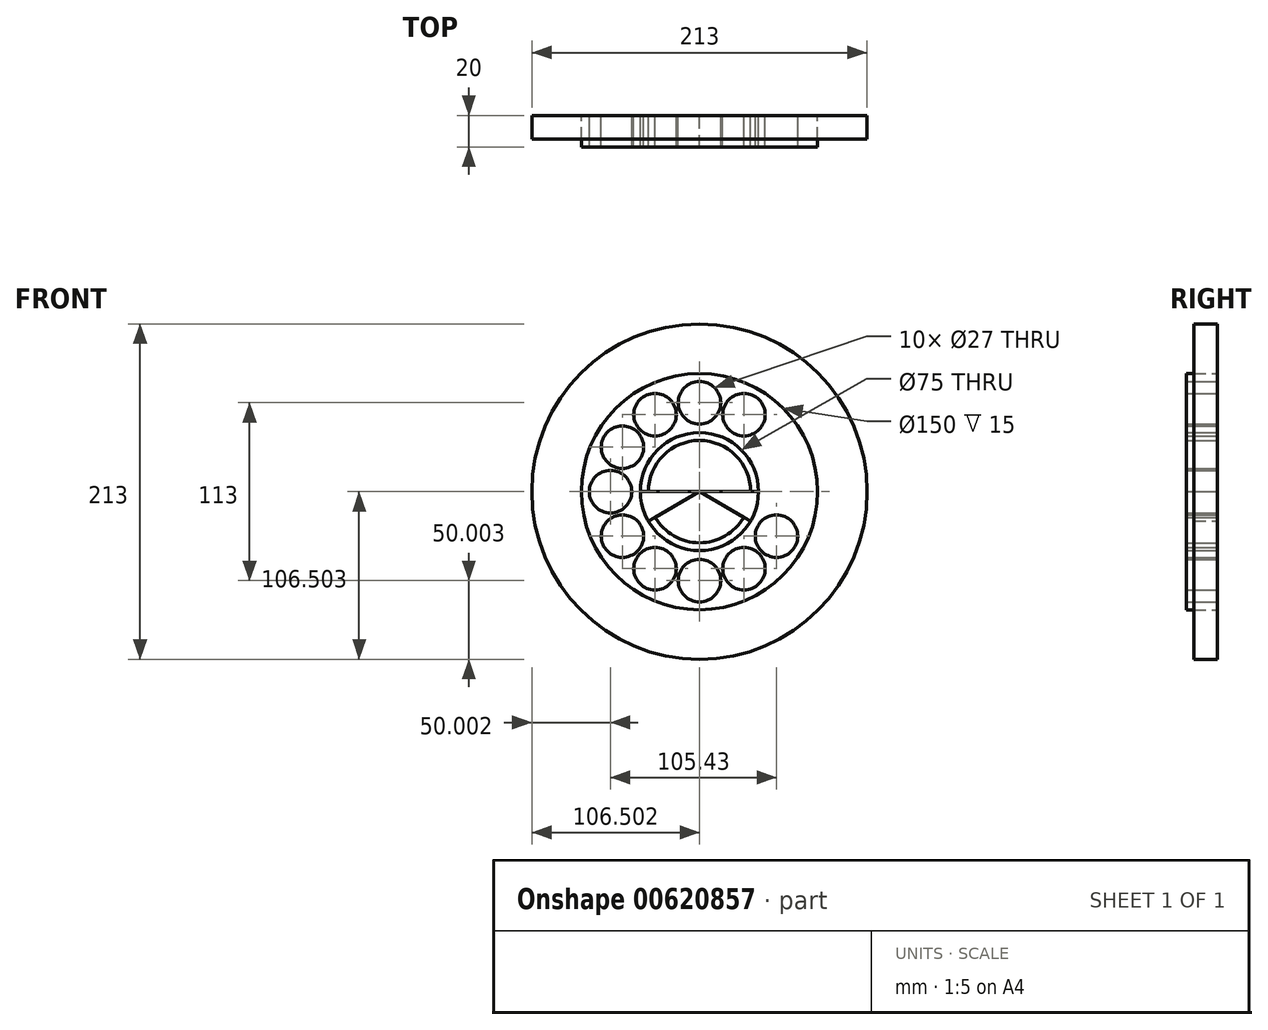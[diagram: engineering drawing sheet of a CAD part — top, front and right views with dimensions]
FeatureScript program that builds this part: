
annotation { "Feature Type Name" : "Feature", "Feature Type Description" : "" }
export const myFeature = defineFeature(function(context is Context, id is Id, definition is map)
    precondition{}
    {
        {
            var Q0;
            Q0=qCreatedBy(makeId("Front.planeOp"),FACE);
            var sketch = newSketch(context, id + "F0", { "sketchPlane" : qUnion([Q0])});
            skCircle(sketch, "E0", {"center": v(-36.97, 6.73) * mm, "radius": 32.5 * mm});
            skCircle(sketch, "E1", {"center": v(-36.97, 6.73) * mm, "radius": 37.5 * mm});
            skCircle(sketch, "E2", {"center": v(-8.72, 55.66) * mm, "radius": 13.5 * mm});
            skCircle(sketch, "E3", {"center": v(-85.9, 35) * mm, "radius": 13.5 * mm});
            skCircle(sketch, "E4", {"center": v(-85.9, -21.52) * mm, "radius": 13.5 * mm});
            skCircle(sketch, "E5", {"center": v(-8.72, -42.2) * mm, "radius": 13.5 * mm});
            skPoint(sketch, "E6.orphan", {"position": v(-36.97, 76.24) * mm});
            skLineSegment(sketch, "E7.trimOffspring", {"start": v(20.03, 6.73) * mm, "end": v(34.08, 6.73) * mm});
            skLineSegment(sketch, "E8.trimOffspring", {"start": v(-36.97, -30.77) * mm, "end": v(-36.97, -54.77) * mm});
            skPoint(sketch, "E9.trimOffspring.end.orphan", {"position": v(-36.97, -60.9) * mm});
            skLineSegment(sketch, "E10", {"start": v(-36.97, 76.24) * mm, "end": v(-36.97, -60.9) * mm});
            skLineSegment(sketch, "E11", {"start": v(-93.47, 6.73) * mm, "end": v(20.03, 6.73) * mm});
            skLineSegment(sketch, "E12", {"start": v(-36.97, 6.73) * mm, "end": v(-2.84, 65.84) * mm});
            skLineSegment(sketch, "E13", {"start": v(-36.97, 6.73) * mm, "end": v(30.96, 45.95) * mm});
            skLineSegment(sketch, "E14", {"start": v(-36.97, 6.73) * mm, "end": v(33.85, -34.15) * mm});
            skLineSegment(sketch, "E15", {"start": v(-36.98, 6.75) * mm, "end": v(0.56, -58.26) * mm});
            skLineSegment(sketch, "E16", {"start": v(0.56, -58.26) * mm, "end": v(-0.88, -59.19) * mm});
            skLineSegment(sketch, "E17", {"start": v(-36.97, 6.73) * mm, "end": v(-72.36, -54.56) * mm});
            skLineSegment(sketch, "E18", {"start": v(-36.97, 6.73) * mm, "end": v(-98.34, -28.7) * mm});
            skLineSegment(sketch, "E19", {"start": v(-36.97, 6.73) * mm, "end": v(-68.98, 62.19) * mm});
            skLineSegment(sketch, "E20", {"start": v(-36.98, 6.75) * mm, "end": v(-93.97, 39.65) * mm});
            skCircle(sketch, "E21", {"center": v(-36.97, 6.73) * mm, "radius": 56.5 * mm, "construction": true});
            skCircle(sketch, "E22", {"center": v(-65.22, 55.66) * mm, "radius": 13.5 * mm});
            skCircle(sketch, "E23", {"center": v(-36.97, 63.23) * mm, "radius": 13.5 * mm});
            skCircle(sketch, "E24", {"center": v(-36.97, 6.73) * mm, "radius": 106.5 * mm});
            skCircle(sketch, "E25", {"center": v(-36.97, -49.77) * mm, "radius": 13.5 * mm});
            skCircle(sketch, "E26", {"center": v(-65.22, -42.2) * mm, "radius": 13.5 * mm});
            skCircle(sketch, "E27", {"center": v(-93.47, 6.73) * mm, "radius": 13.5 * mm});
            skCircle(sketch, "E28", {"center": v(11.96, -21.52) * mm, "radius": 13.5 * mm});
            skCircle(sketch, "E29", {"center": v(-36.97, 6.73) * mm, "radius": 75 * mm});
            skSolve(sketch);
        }
        {
            var Q0;
            {var subQ0=sQuery(id+"F0.wireOp",EDGE,"E12");var subQ1=sQuery(id+"F0.wireOp",EDGE,"E0");var subQ2=makeQuery(id+"F0.imprint","INTERSECT",VERTEX,{"derivedFrom":[subQ1,subQ0]});Q0=makeQuery(id+"F0.imprint","IMPRINT",FACE,{"disambiguationData":[TD([[makeQuery(id+"F0.imprint","IMPRINT",EDGE,{"disambiguationData":[TD([[subQ2,-1.0]])],"derivedFrom":subQ1}),-1.0]])]});}
            var Q1;
            {var subQ0=sQuery(id+"F0.wireOp",EDGE,"E13");var subQ1=sQuery(id+"F0.wireOp",EDGE,"E0");var subQ2=makeQuery(id+"F0.imprint","INTERSECT",VERTEX,{"derivedFrom":[subQ1,subQ0]});Q1=makeQuery(id+"F0.imprint","IMPRINT",FACE,{"disambiguationData":[TD([[makeQuery(id+"F0.imprint","IMPRINT",EDGE,{"disambiguationData":[TD([[subQ2,-1.0]])],"derivedFrom":subQ1}),-1.0]])]});}
            var Q2;
            {var subQ0=sQuery(id+"F0.wireOp",EDGE,"E13");var subQ1=sQuery(id+"F0.wireOp",EDGE,"E0");var subQ2=makeQuery(id+"F0.imprint","INTERSECT",VERTEX,{"derivedFrom":[subQ1,subQ0]});Q2=makeQuery(id+"F0.imprint","IMPRINT",FACE,{"disambiguationData":[TD([[makeQuery(id+"F0.imprint","IMPRINT",EDGE,{"disambiguationData":[TD([[subQ2,1.0]])],"derivedFrom":subQ1}),-1.0]])]});}
            var Q3;
            {var subQ0=sQuery(id+"F0.wireOp",EDGE,"E10");var subQ1=sQuery(id+"F0.wireOp",EDGE,"E0");var subQ2=makeQuery(id+"F0.imprint","INTERSECT",VERTEX,{"disambiguationData":[OD(0.0)],"derivedFrom":[subQ1,subQ0]});Q3=makeQuery(id+"F0.imprint","IMPRINT",FACE,{"disambiguationData":[TD([[makeQuery(id+"F0.imprint","IMPRINT",EDGE,{"disambiguationData":[TD([[subQ2,-1.0]])],"derivedFrom":subQ1}),-1.0]])]});}
            var Q4;
            {var subQ0=sQuery(id+"F0.wireOp",EDGE,"E19");var subQ1=sQuery(id+"F0.wireOp",EDGE,"E0");var subQ2=makeQuery(id+"F0.imprint","INTERSECT",VERTEX,{"derivedFrom":[subQ1,subQ0]});Q4=makeQuery(id+"F0.imprint","IMPRINT",FACE,{"disambiguationData":[TD([[makeQuery(id+"F0.imprint","IMPRINT",EDGE,{"disambiguationData":[TD([[subQ2,-1.0]])],"derivedFrom":subQ1}),-1.0]])]});}
            var Q5;
            {var subQ0=sQuery(id+"F0.wireOp",EDGE,"E20");var subQ1=sQuery(id+"F0.wireOp",EDGE,"E0");var subQ2=makeQuery(id+"F0.imprint","INTERSECT",VERTEX,{"derivedFrom":[subQ1,subQ0]});Q5=makeQuery(id+"F0.imprint","IMPRINT",FACE,{"disambiguationData":[TD([[makeQuery(id+"F0.imprint","IMPRINT",EDGE,{"disambiguationData":[TD([[subQ2,-1.0]])],"derivedFrom":subQ1}),-1.0]])]});}
            var Q6;
            {var subQ0=sQuery(id+"F0.wireOp",EDGE,"E11");var subQ1=sQuery(id+"F0.wireOp",EDGE,"E0");var subQ2=makeQuery(id+"F0.imprint","INTERSECT",VERTEX,{"disambiguationData":[OD(1.0)],"derivedFrom":[subQ1,subQ0]});Q6=makeQuery(id+"F0.imprint","IMPRINT",FACE,{"disambiguationData":[TD([[makeQuery(id+"F0.imprint","IMPRINT",EDGE,{"disambiguationData":[TD([[subQ2,-1.0]])],"derivedFrom":subQ1}),-1.0]])]});}
            var Q7;
            {var subQ0=sQuery(id+"F0.wireOp",EDGE,"E18");var subQ1=sQuery(id+"F0.wireOp",EDGE,"E0");var subQ2=makeQuery(id+"F0.imprint","INTERSECT",VERTEX,{"derivedFrom":[subQ1,subQ0]});Q7=makeQuery(id+"F0.imprint","IMPRINT",FACE,{"disambiguationData":[TD([[makeQuery(id+"F0.imprint","IMPRINT",EDGE,{"disambiguationData":[TD([[subQ2,-1.0]])],"derivedFrom":subQ1}),-1.0]])]});}
            var Q8;
            {var subQ0=sQuery(id+"F0.wireOp",EDGE,"E17");var subQ1=sQuery(id+"F0.wireOp",EDGE,"E0");var subQ2=makeQuery(id+"F0.imprint","INTERSECT",VERTEX,{"derivedFrom":[subQ1,subQ0]});Q8=makeQuery(id+"F0.imprint","IMPRINT",FACE,{"disambiguationData":[TD([[makeQuery(id+"F0.imprint","IMPRINT",EDGE,{"disambiguationData":[TD([[subQ2,-1.0]])],"derivedFrom":subQ1}),-1.0]])]});}
            var Q9;
            {var subQ0=sQuery(id+"F0.wireOp",EDGE,"E10");var subQ1=sQuery(id+"F0.wireOp",EDGE,"E0");var subQ2=makeQuery(id+"F0.imprint","INTERSECT",VERTEX,{"disambiguationData":[OD(1.0)],"derivedFrom":[subQ1,subQ0]});Q9=makeQuery(id+"F0.imprint","IMPRINT",FACE,{"disambiguationData":[TD([[makeQuery(id+"F0.imprint","IMPRINT",EDGE,{"disambiguationData":[TD([[subQ2,-1.0]])],"derivedFrom":subQ1}),-1.0]])]});}
            var Q10;
            {var subQ0=sQuery(id+"F0.wireOp",EDGE,"E11");var subQ1=sQuery(id+"F0.wireOp",EDGE,"E0");var subQ2=makeQuery(id+"F0.imprint","INTERSECT",VERTEX,{"disambiguationData":[OD(0.0)],"derivedFrom":[subQ1,subQ0]});Q10=makeQuery(id+"F0.imprint","IMPRINT",FACE,{"disambiguationData":[TD([[makeQuery(id+"F0.imprint","IMPRINT",EDGE,{"disambiguationData":[TD([[subQ2,1.0]])],"derivedFrom":subQ1}),-1.0]])]});}
            var Q11;
            Q11=makeQuery(id+"F0.imprint","IMPRINT",FACE,{"disambiguationData":[TD([[makeQuery(id+"F0.imprint","IMPRINT",EDGE,{"derivedFrom":sQuery(id+"F0.wireOp",EDGE,"E24")}),1.0]])]});
            var Q12;
            {var subQ0=sQuery(id+"F0.wireOp",EDGE,"E15");var subQ1=sQuery(id+"F0.wireOp",EDGE,"E0");var subQ2=makeQuery(id+"F0.imprint","INTERSECT",VERTEX,{"derivedFrom":[subQ1,subQ0]});Q12=makeQuery(id+"F0.imprint","IMPRINT",FACE,{"disambiguationData":[TD([[makeQuery(id+"F0.imprint","IMPRINT",EDGE,{"disambiguationData":[TD([[subQ2,-1.0]])],"derivedFrom":subQ1}),-1.0]])]});}
            var Q13;
            Q13=makeQuery(id+"F0.imprint","IMPRINT",FACE,{"disambiguationData":[TD([[makeQuery(id+"F0.imprint","IMPRINT",EDGE,{"derivedFrom":sQuery(id+"F0.wireOp",EDGE,"E22")}),1.0]])]});
            var Q14;
            Q14=makeQuery(id+"F0.imprint","IMPRINT",FACE,{"disambiguationData":[TD([[makeQuery(id+"F0.imprint","IMPRINT",EDGE,{"derivedFrom":sQuery(id+"F0.wireOp",EDGE,"E3")}),1.0]])]});
            var Q15;
            Q15=makeQuery(id+"F0.imprint","IMPRINT",FACE,{"disambiguationData":[TD([[makeQuery(id+"F0.imprint","IMPRINT",EDGE,{"derivedFrom":sQuery(id+"F0.wireOp",EDGE,"E27")}),1.0]])]});
            var Q16;
            Q16=makeQuery(id+"F0.imprint","IMPRINT",FACE,{"disambiguationData":[TD([[makeQuery(id+"F0.imprint","IMPRINT",EDGE,{"derivedFrom":sQuery(id+"F0.wireOp",EDGE,"E23")}),1.0]])]});
            var Q17;
            Q17=makeQuery(id+"F0.imprint","IMPRINT",FACE,{"disambiguationData":[TD([[makeQuery(id+"F0.imprint","IMPRINT",EDGE,{"derivedFrom":sQuery(id+"F0.wireOp",EDGE,"E2")}),1.0]])]});
            var Q18;
            {var subQ0=sQuery(id+"F0.wireOp",EDGE,"E18");var subQ1=sQuery(id+"F0.wireOp",EDGE,"E4");var subQ2=makeQuery(id+"F0.imprint","INTERSECT",VERTEX,{"disambiguationData":[OD(0.0)],"derivedFrom":[subQ1,subQ0]});Q18=makeQuery(id+"F0.imprint","IMPRINT",FACE,{"disambiguationData":[TD([[makeQuery(id+"F0.imprint","IMPRINT",EDGE,{"disambiguationData":[TD([[subQ2,1.0]])],"derivedFrom":subQ1}),1.0]])]});}
            var Q19;
            {var subQ0=sQuery(id+"F0.wireOp",EDGE,"E18");var subQ1=sQuery(id+"F0.wireOp",EDGE,"E4");var subQ2=makeQuery(id+"F0.imprint","INTERSECT",VERTEX,{"disambiguationData":[OD(0.0)],"derivedFrom":[subQ1,subQ0]});Q19=makeQuery(id+"F0.imprint","IMPRINT",FACE,{"disambiguationData":[TD([[makeQuery(id+"F0.imprint","IMPRINT",EDGE,{"disambiguationData":[TD([[subQ2,-1.0]])],"derivedFrom":subQ1}),1.0]])]});}
            var Q20;
            {var subQ0=sQuery(id+"F0.wireOp",EDGE,"E26");var subQ1=sQuery(id+"F0.wireOp",EDGE,"E17");var subQ2=makeQuery(id+"F0.imprint","INTERSECT",VERTEX,{"disambiguationData":[OD(0.0)],"derivedFrom":[subQ1,subQ0]});Q20=makeQuery(id+"F0.imprint","IMPRINT",FACE,{"disambiguationData":[TD([[makeQuery(id+"F0.imprint","IMPRINT",EDGE,{"disambiguationData":[TD([[subQ2,1.0]])],"derivedFrom":subQ1}),1.0]])]});}
            var Q21;
            {var subQ0=sQuery(id+"F0.wireOp",EDGE,"E26");var subQ1=sQuery(id+"F0.wireOp",EDGE,"E17");var subQ2=makeQuery(id+"F0.imprint","INTERSECT",VERTEX,{"disambiguationData":[OD(0.0)],"derivedFrom":[subQ1,subQ0]});Q21=makeQuery(id+"F0.imprint","IMPRINT",FACE,{"disambiguationData":[TD([[makeQuery(id+"F0.imprint","IMPRINT",EDGE,{"disambiguationData":[TD([[subQ2,1.0]])],"derivedFrom":subQ1}),-1.0]])]});}
            var Q22;
            Q22=makeQuery(id+"F0.imprint","IMPRINT",FACE,{"disambiguationData":[TD([[makeQuery(id+"F0.imprint","IMPRINT",EDGE,{"derivedFrom":sQuery(id+"F0.wireOp",EDGE,"E25")}),1.0]])]});
            var Q23;
            {var subQ0=sQuery(id+"F0.wireOp",EDGE,"E15");var subQ1=sQuery(id+"F0.wireOp",EDGE,"E5");var subQ2=makeQuery(id+"F0.imprint","INTERSECT",VERTEX,{"disambiguationData":[OD(0.0)],"derivedFrom":[subQ1,subQ0]});Q23=makeQuery(id+"F0.imprint","IMPRINT",FACE,{"disambiguationData":[TD([[makeQuery(id+"F0.imprint","IMPRINT",EDGE,{"disambiguationData":[TD([[subQ2,-1.0]])],"derivedFrom":subQ1}),1.0]])]});}
            var Q24;
            {var subQ0=sQuery(id+"F0.wireOp",EDGE,"E15");var subQ1=sQuery(id+"F0.wireOp",EDGE,"E5");var subQ2=makeQuery(id+"F0.imprint","INTERSECT",VERTEX,{"disambiguationData":[OD(0.0)],"derivedFrom":[subQ1,subQ0]});Q24=makeQuery(id+"F0.imprint","IMPRINT",FACE,{"disambiguationData":[TD([[makeQuery(id+"F0.imprint","IMPRINT",EDGE,{"disambiguationData":[TD([[subQ2,1.0]])],"derivedFrom":subQ1}),1.0]])]});}
            var Q25;
            {var subQ0=sQuery(id+"F0.wireOp",EDGE,"E28");var subQ1=sQuery(id+"F0.wireOp",EDGE,"E14");var subQ2=makeQuery(id+"F0.imprint","INTERSECT",VERTEX,{"disambiguationData":[OD(0.0)],"derivedFrom":[subQ1,subQ0]});Q25=makeQuery(id+"F0.imprint","IMPRINT",FACE,{"disambiguationData":[TD([[makeQuery(id+"F0.imprint","IMPRINT",EDGE,{"disambiguationData":[TD([[subQ2,-1.0]])],"derivedFrom":subQ1}),-1.0]])]});}
            var Q26;
            {var subQ0=sQuery(id+"F0.wireOp",EDGE,"E28");var subQ1=sQuery(id+"F0.wireOp",EDGE,"E14");var subQ2=makeQuery(id+"F0.imprint","INTERSECT",VERTEX,{"disambiguationData":[OD(0.0)],"derivedFrom":[subQ1,subQ0]});Q26=makeQuery(id+"F0.imprint","IMPRINT",FACE,{"disambiguationData":[TD([[makeQuery(id+"F0.imprint","IMPRINT",EDGE,{"disambiguationData":[TD([[subQ2,-1.0]])],"derivedFrom":subQ1}),1.0]])]});}
            extrude(context, id + "F1", {"entities" : qUnion([Q0, Q1, Q2, Q3, Q4, Q5, Q6, Q7, Q8, Q9, Q10, Q11, Q12, Q13, Q14, Q15, Q16, Q17, Q18, Q19, Q20, Q21, Q22, Q23, Q24, Q25, Q26]), "depth" : 15 * mm, "offsetDistance" : 25 * mm});
        }
        {
            var Q0;
            Q0=makeQuery(id+"F0.imprint","IMPRINT",FACE,{"disambiguationData":[TD([[makeQuery(id+"F0.imprint","IMPRINT",EDGE,{"derivedFrom":sQuery(id+"F0.wireOp",EDGE,"E2")}),-1.0]])]});
            var Q1;
            {var subQ1=sQuery(id+"F0.wireOp",EDGE,"E1");var subQ5=makeQuery(id+"F0.imprint","INTERSECT",VERTEX,{"disambiguationData":[OD(0.0)],"derivedFrom":[subQ1,sQuery(id+"F0.wireOp",EDGE,"E11")]});Q1=makeQuery(id+"F0.imprint","IMPRINT",FACE,{"disambiguationData":[TD([[makeQuery(id+"F0.imprint","IMPRINT",EDGE,{"disambiguationData":[TD([[subQ5,-1.0]])],"derivedFrom":subQ1}),-1.0]])]});}
            var Q2;
            {var subQ1=sQuery(id+"F0.wireOp",EDGE,"E1");var subQ5=sQuery(id+"F0.wireOp",EDGE,"E15");var subQ12=makeQuery(id+"F0.imprint","INTERSECT",VERTEX,{"derivedFrom":[subQ1,subQ5]});Q2=makeQuery(id+"F0.imprint","IMPRINT",FACE,{"disambiguationData":[TD([[makeQuery(id+"F0.imprint","IMPRINT",EDGE,{"disambiguationData":[TD([[subQ12,-1.0]])],"derivedFrom":subQ1}),-1.0]])]});}
            var Q3;
            {var subQ0=sQuery(id+"F0.wireOp",EDGE,"E12");var subQ1=sQuery(id+"F0.wireOp",EDGE,"E0");var subQ2=makeQuery(id+"F0.imprint","INTERSECT",VERTEX,{"derivedFrom":[subQ1,subQ0]});Q3=makeQuery(id+"F0.imprint","IMPRINT",FACE,{"disambiguationData":[TD([[makeQuery(id+"F0.imprint","IMPRINT",EDGE,{"disambiguationData":[TD([[subQ2,-1.0]])],"derivedFrom":subQ1}),1.0]])]});}
            var Q4;
            {var subQ0=sQuery(id+"F0.wireOp",EDGE,"E10");var subQ1=sQuery(id+"F0.wireOp",EDGE,"E0");var subQ2=makeQuery(id+"F0.imprint","INTERSECT",VERTEX,{"disambiguationData":[OD(0.0)],"derivedFrom":[subQ1,subQ0]});Q4=makeQuery(id+"F0.imprint","IMPRINT",FACE,{"disambiguationData":[TD([[makeQuery(id+"F0.imprint","IMPRINT",EDGE,{"disambiguationData":[TD([[subQ2,-1.0]])],"derivedFrom":subQ1}),1.0]])]});}
            var Q5;
            {var subQ0=sQuery(id+"F0.wireOp",EDGE,"E19");var subQ1=sQuery(id+"F0.wireOp",EDGE,"E0");var subQ2=makeQuery(id+"F0.imprint","INTERSECT",VERTEX,{"derivedFrom":[subQ1,subQ0]});Q5=makeQuery(id+"F0.imprint","IMPRINT",FACE,{"disambiguationData":[TD([[makeQuery(id+"F0.imprint","IMPRINT",EDGE,{"disambiguationData":[TD([[subQ2,-1.0]])],"derivedFrom":subQ1}),1.0]])]});}
            var Q6;
            {var subQ0=sQuery(id+"F0.wireOp",EDGE,"E11");var subQ1=sQuery(id+"F0.wireOp",EDGE,"E0");var subQ2=makeQuery(id+"F0.imprint","INTERSECT",VERTEX,{"disambiguationData":[OD(1.0)],"derivedFrom":[subQ1,subQ0]});Q6=makeQuery(id+"F0.imprint","IMPRINT",FACE,{"disambiguationData":[TD([[makeQuery(id+"F0.imprint","IMPRINT",EDGE,{"disambiguationData":[TD([[subQ2,-1.0]])],"derivedFrom":subQ1}),1.0]])]});}
            var Q7;
            {var subQ0=sQuery(id+"F0.wireOp",EDGE,"E18");var subQ1=sQuery(id+"F0.wireOp",EDGE,"E0");var subQ2=makeQuery(id+"F0.imprint","INTERSECT",VERTEX,{"derivedFrom":[subQ1,subQ0]});Q7=makeQuery(id+"F0.imprint","IMPRINT",FACE,{"disambiguationData":[TD([[makeQuery(id+"F0.imprint","IMPRINT",EDGE,{"disambiguationData":[TD([[subQ2,-1.0]])],"derivedFrom":subQ1}),1.0]])]});}
            var Q8;
            {var subQ0=sQuery(id+"F0.wireOp",EDGE,"E17");var subQ1=sQuery(id+"F0.wireOp",EDGE,"E0");var subQ2=makeQuery(id+"F0.imprint","INTERSECT",VERTEX,{"derivedFrom":[subQ1,subQ0]});Q8=makeQuery(id+"F0.imprint","IMPRINT",FACE,{"disambiguationData":[TD([[makeQuery(id+"F0.imprint","IMPRINT",EDGE,{"disambiguationData":[TD([[subQ2,-1.0]])],"derivedFrom":subQ1}),1.0]])]});}
            var Q9;
            {var subQ0=sQuery(id+"F0.wireOp",EDGE,"E10");var subQ1=sQuery(id+"F0.wireOp",EDGE,"E0");var subQ2=makeQuery(id+"F0.imprint","INTERSECT",VERTEX,{"disambiguationData":[OD(1.0)],"derivedFrom":[subQ1,subQ0]});Q9=makeQuery(id+"F0.imprint","IMPRINT",FACE,{"disambiguationData":[TD([[makeQuery(id+"F0.imprint","IMPRINT",EDGE,{"disambiguationData":[TD([[subQ2,-1.0]])],"derivedFrom":subQ1}),1.0]])]});}
            var Q10;
            {var subQ0=sQuery(id+"F0.wireOp",EDGE,"E20");var subQ1=sQuery(id+"F0.wireOp",EDGE,"E0");var subQ2=makeQuery(id+"F0.imprint","INTERSECT",VERTEX,{"derivedFrom":[subQ1,subQ0]});Q10=makeQuery(id+"F0.imprint","IMPRINT",FACE,{"disambiguationData":[TD([[makeQuery(id+"F0.imprint","IMPRINT",EDGE,{"disambiguationData":[TD([[subQ2,-1.0]])],"derivedFrom":subQ1}),1.0]])]});}
            var Q11;
            {var subQ0=sQuery(id+"F0.wireOp",EDGE,"E13");var subQ1=sQuery(id+"F0.wireOp",EDGE,"E0");var subQ2=makeQuery(id+"F0.imprint","INTERSECT",VERTEX,{"derivedFrom":[subQ1,subQ0]});Q11=makeQuery(id+"F0.imprint","IMPRINT",FACE,{"disambiguationData":[TD([[makeQuery(id+"F0.imprint","IMPRINT",EDGE,{"disambiguationData":[TD([[subQ2,-1.0]])],"derivedFrom":subQ1}),1.0]])]});}
            var Q12;
            {var subQ0=sQuery(id+"F0.wireOp",EDGE,"E13");var subQ1=sQuery(id+"F0.wireOp",EDGE,"E0");var subQ2=makeQuery(id+"F0.imprint","INTERSECT",VERTEX,{"derivedFrom":[subQ1,subQ0]});Q12=makeQuery(id+"F0.imprint","IMPRINT",FACE,{"disambiguationData":[TD([[makeQuery(id+"F0.imprint","IMPRINT",EDGE,{"disambiguationData":[TD([[subQ2,1.0]])],"derivedFrom":subQ1}),1.0]])]});}
            var Q13;
            {var subQ0=sQuery(id+"F0.wireOp",EDGE,"E11");var subQ1=sQuery(id+"F0.wireOp",EDGE,"E0");var subQ2=makeQuery(id+"F0.imprint","INTERSECT",VERTEX,{"disambiguationData":[OD(0.0)],"derivedFrom":[subQ1,subQ0]});Q13=makeQuery(id+"F0.imprint","IMPRINT",FACE,{"disambiguationData":[TD([[makeQuery(id+"F0.imprint","IMPRINT",EDGE,{"disambiguationData":[TD([[subQ2,1.0]])],"derivedFrom":subQ1}),1.0]])]});}
            var Q14;
            {var subQ0=sQuery(id+"F0.wireOp",EDGE,"E15");var subQ1=sQuery(id+"F0.wireOp",EDGE,"E0");var subQ2=makeQuery(id+"F0.imprint","INTERSECT",VERTEX,{"derivedFrom":[subQ1,subQ0]});Q14=makeQuery(id+"F0.imprint","IMPRINT",FACE,{"disambiguationData":[TD([[makeQuery(id+"F0.imprint","IMPRINT",EDGE,{"disambiguationData":[TD([[subQ2,-1.0]])],"derivedFrom":subQ1}),1.0]])]});}
            extrude(context, id + "F2", {"entities" : qUnion([Q0, Q1, Q2, Q3, Q4, Q5, Q6, Q7, Q8, Q9, Q10, Q11, Q12, Q13, Q14]), "depth" : 20 * mm, "offsetDistance" : 25 * mm});
        }
    });
